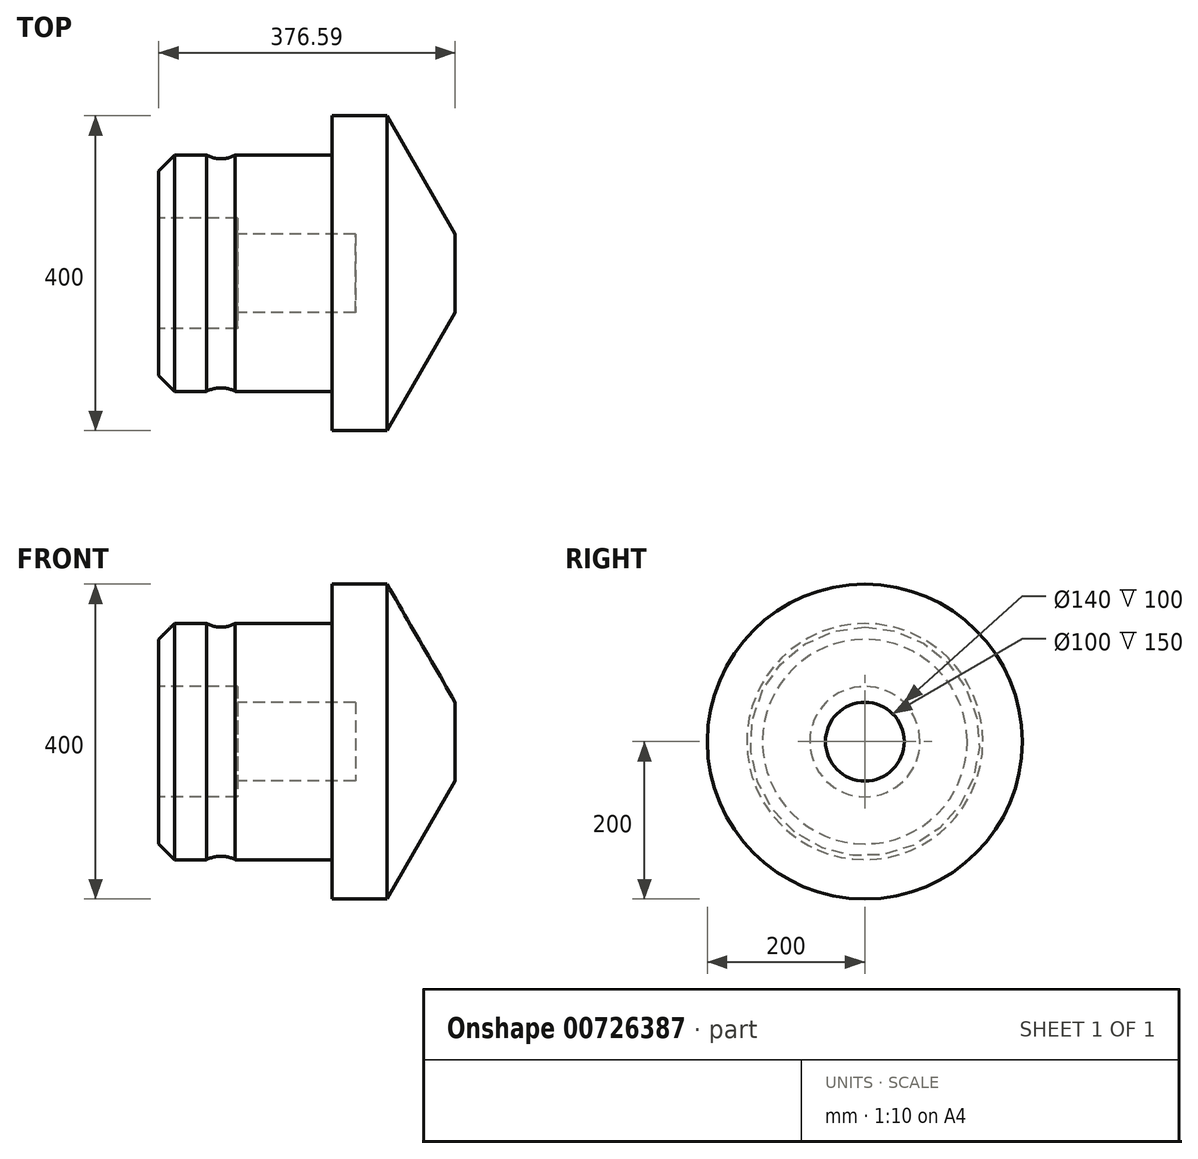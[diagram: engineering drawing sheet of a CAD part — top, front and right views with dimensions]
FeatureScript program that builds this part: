
annotation { "Feature Type Name" : "Feature", "Feature Type Description" : "" }
export const myFeature = defineFeature(function(context is Context, id is Id, definition is map)
    precondition{}
    {
        {
            var Q0;
            Q0=qCreatedBy(makeId("Front.planeOp"),FACE);
            var sketch = newSketch(context, id + "F0", { "sketchPlane" : qUnion([Q0])});
            skLineSegment(sketch, "E0", {"start": v(0, 0) * mm, "end": v(0, 50) * mm});
            skLineSegment(sketch, "E1", {"start": v(0, 50) * mm, "end": v(-86.6, 200) * mm});
            skLineSegment(sketch, "E2", {"start": v(-86.6, 200) * mm, "end": v(-156.6, 200) * mm});
            skLineSegment(sketch, "E3", {"start": v(-156.6, 200) * mm, "end": v(-156.6, 150) * mm});
            skLineSegment(sketch, "E4", {"start": v(-156.6, 150) * mm, "end": v(-276.46, 150) * mm});
            skLineSegment(sketch, "E5", {"start": v(-356.6, 150) * mm, "end": v(-376.59, 130.02) * mm});
            skLineSegment(sketch, "E6", {"start": v(-376.59, 130.02) * mm, "end": v(-376.59, 70) * mm});
            skLineSegment(sketch, "E7", {"start": v(-376.59, 70) * mm, "end": v(-276.59, 70) * mm});
            skLineSegment(sketch, "E8", {"start": v(-276.59, 70) * mm, "end": v(-276.59, 50) * mm});
            skLineSegment(sketch, "E9", {"start": v(-276.59, 50) * mm, "end": v(-126.59, 50) * mm});
            skLineSegment(sketch, "E10", {"start": v(-126.59, 0) * mm, "end": v(0, 0) * mm});
            skLineSegment(sketch, "E11", {"start": v(-126.59, 0) * mm, "end": v(-126.59, 50) * mm});
            skLineSegment(sketch, "E12.trimOffspring", {"start": v(-315.71, 150) * mm, "end": v(-356.6, 150) * mm});
            skLineSegment(sketch, "E13", {"start": v(-315.71, 150) * mm, "end": v(-276.46, 150) * mm});
            skCircle(sketch, "E14", {"center": v(-297.58, 183.95) * mm, "radius": 38.5 * mm});
            skSolve(sketch);
        }
        {
            var Q0;
            Q0=makeQuery(id+"F0.imprint","IMPRINT",FACE,{"disambiguationData":[TD([[makeQuery(id+"F0.imprint","IMPRINT",EDGE,{"derivedFrom":sQuery(id+"F0.wireOp",EDGE,"E0")}),1.0]])]});
            var Q1;
            Q1=sQuery(id+"F0.wireOp",EDGE,"E10");
            revolve(context, id + "F1", {"surfaceOperationType" : NewSurfaceOperationType.NEW, "entities" : qUnion([Q0]), "axis" : qUnion([Q1]), "revolveType" : RevolveType.FULL});
        }
    });
